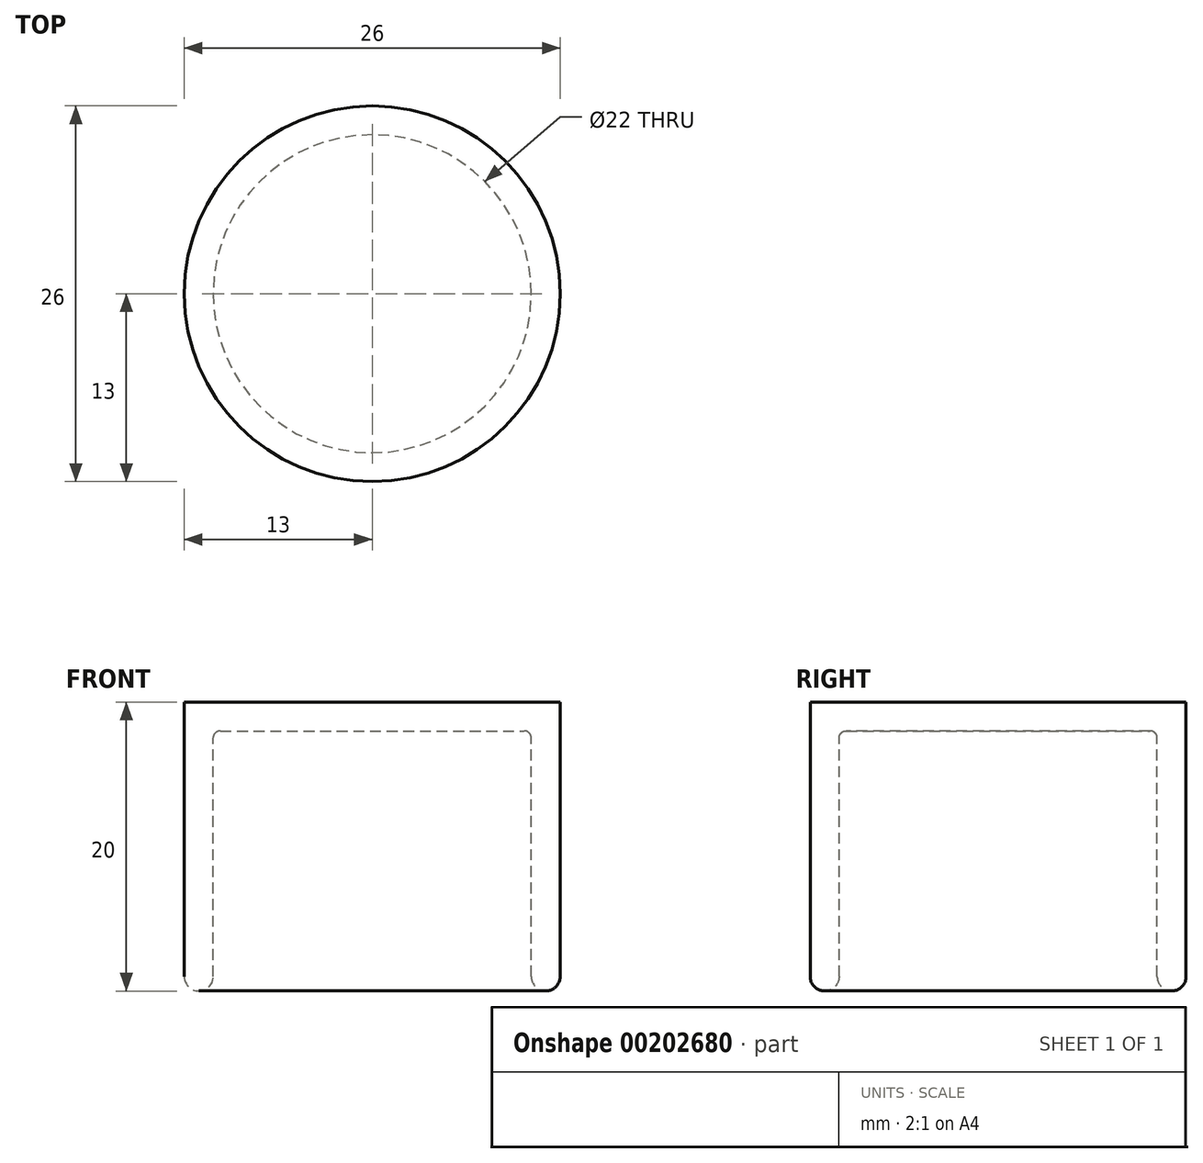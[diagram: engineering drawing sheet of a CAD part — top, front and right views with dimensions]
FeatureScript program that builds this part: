
annotation { "Feature Type Name" : "Feature", "Feature Type Description" : "" }
export const myFeature = defineFeature(function(context is Context, id is Id, definition is map)
    precondition{}
    {
        {
            var Q0;
            Q0=qCreatedBy(makeId("Front.planeOp"),FACE);
            var sketch = newSketch(context, id + "F0", { "sketchPlane" : qUnion([Q0])});
            skLineSegment(sketch, "E0.bottom", {"start": v(-5, 17.14) * mm, "end": v(8, 17.14) * mm});
            skLineSegment(sketch, "E0.top", {"start": v(-5, -2.86) * mm, "end": v(-3, -2.86) * mm});
            skLineSegment(sketch, "E0.left", {"start": v(-5, 17.14) * mm, "end": v(-5, -2.86) * mm});
            skLineSegment(sketch, "E0.right", {"start": v(8, 17.14) * mm, "end": v(8, 15.14) * mm});
            skLineSegment(sketch, "E1.0", {"start": v(-3, 15.14) * mm, "end": v(-3, -2.86) * mm});
            skLineSegment(sketch, "E1.1", {"start": v(-3, 15.14) * mm, "end": v(8, 15.14) * mm});
            skSolve(sketch);
        }
        {
            var Q0;
            Q0 = qSketchRegion(id + "F0", true);
            var Q1;
            Q1=sQuery(id+"F0.wireOp",EDGE,"E0.right");
            revolve(context, id + "F1", {"entities" : qUnion([Q0]), "axis" : qUnion([Q1]), "revolveType" : RevolveType.FULL});
        }
        {
            var Q0;
            Q0=makeQuery(id+"F1.opRevolve","SWEPT_EDGE",EDGE,{"disambiguationData":[OSD([sQuery(id+"F0.wireOp",EDGE,"E1.0"),sQuery(id+"F0.wireOp",EDGE,"E1.1")])]});
            fillet(context, id + "F2", {"entities" : qUnion([Q0]), "radius" : 0.5 * mm, "tangentPropagation" : true, "allowEdgeOverflow" : false});
        }
        {
            var Q0;
            Q0=makeQuery(id+"F1.opRevolve","SWEPT_FACE",FACE,{"disambiguationData":[OSD([sQuery(id+"F0.wireOp",EDGE,"E0.top")])]});
            fillet(context, id + "F3", {"entities" : qUnion([Q0]), "radius" : 1 * mm, "tangentPropagation" : true, "allowEdgeOverflow" : false});
        }
    });
